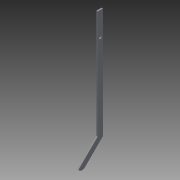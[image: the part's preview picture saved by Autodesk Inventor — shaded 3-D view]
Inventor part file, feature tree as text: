
AUTODESK INVENTOR PART (.ipt)
format: ipt  version: 2013 (Build 170138000, 138)  size: 141,312 bytes
history: native  units: in
note: dims shown in document units (in); Inventor stores cm internally (conversion verified against a paired STEP export)
features: extrude x7, sketch x7
ambient origin geometry x8: Origin, YZ Plane, XZ Plane, XY Plane, X Axis, Y Axis, Z Axis, Center Point
bodies: Solid1 (feature_tree)
feature tree (14):
  extrude  "Extrusion1"  Depth=0.5in
  extrude  "Extrusion2"  Depth=0.5in
  extrude  "Extrusion3"  Depth=16.484in
  extrude  "Extrusion4"  Depth=5.14in
  extrude  "Extrusion5"  Depth=1.0in
  extrude  "Extrusion8"  Depth=6.0in
  extrude  "Extrusion9"  Depth=1.0in
  sketch  "Sketch1"  dims[d0=0.25in d1=0.5in]
  sketch  "Sketch2"  dims[d2=0.0in d3=0.5in]
  sketch  "Sketch3"  dims[d4=90.0deg d5=16.484in]
  sketch  "Sketch4"  dims[d6=1.0in d7=5.14in]
  sketch  "Sketch5"  dims[d8=135.0deg d9=1.0in]
  sketch  "Sketch8"  dims[d10=90.0deg d11=6.0in]
  sketch  "Sketch9"  dims[d12=90.0deg d13=1.0in d14=180.0deg d15=1.0in d16=0.0in d17=0.25in d18=0.75in d19=1.0in d20=0.0in d21=5.0in d22=0.0in d23=0.75in d24=0.0in d25=1.0in d26=5.0in d27=5.0in d28=0.0in d43=4.0in d44=0.0in d45=0.5in d46=1.0in d47=0.0in]
